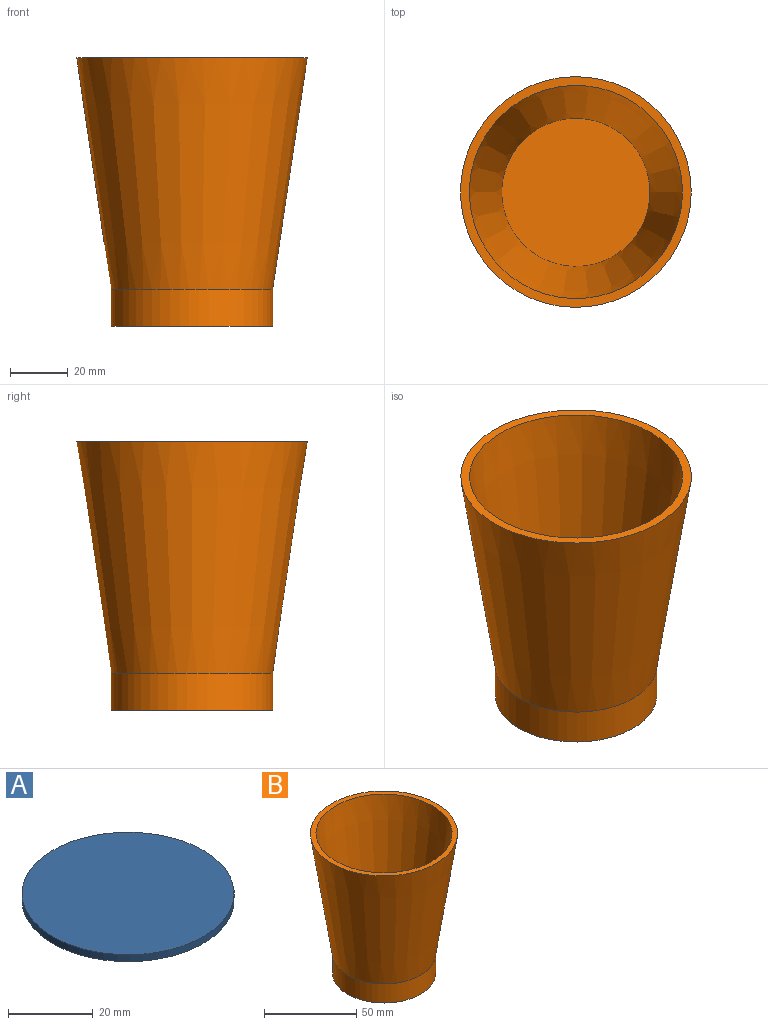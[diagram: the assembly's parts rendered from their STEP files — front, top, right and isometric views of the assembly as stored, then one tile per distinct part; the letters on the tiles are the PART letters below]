
ASSEMBLY  parts=2 mates=1
PART A: 3 faces, bbox 50x50x2 mm
  f0: cylinder r=25mm len=50mm, axis (0,0,-1), area 314.2mm2, adj f1,f2
  f1: plane 50x50mm, normal (0,0,1), area 1963.5mm2, adj f0
  f2: plane 50x50mm, normal (0,0,-1), area 1963.5mm2, adj f0
PART B: 11 faces, bbox 80x80x93 mm
  f0: cylinder r=28mm len=56mm, axis (0,0,-1), area 2234.3mm2, adj f1,f5
  f1: plane 56x56mm, normal (0,0,-1), area 499.5mm2, adj f0,f2
  f2: cylinder r=25mm len=50mm, axis (0,0,-1), area 785.4mm2, adj f1,f3
  f3: plane 50x50mm, normal (0,0,-1), area 1963.5mm2, adj f2
  f4: plane 80x80mm, normal (0,0,1), area 733.4mm2, adj f5,f6
  f5: cone r=40mm half-angle=8.5deg, axis (0,0,1), area 17344.8mm2, adj f0,f4
  f6: cone r=37.03mm half-angle=8.5deg, axis (0,0,1), area 15007.4mm2, adj f4,f7
  f7: plane 51.4x51.4mm, normal (0,0,1), area 2075mm2, adj f6
  f8: cone r=0mm half-angle=89.3deg, axis (0,0,1), area 1963.7mm2, adj f10
  f9: plane 50x50mm, normal (0,0,1), area 1963.5mm2, adj f10
  f10: cylinder r=25mm len=50mm, axis (0,0,-1), area 773.3mm2, adj f8,f9
PLACE A rot(axis=(1,0,0),180deg) t=(-48.58,-19.28,-31.34)mm
PLACE B t=(-48.58,-19.28,-36.34)mm
MATE planar A.f0 <-> B.f2  axis (0,0,1) through (-48.58,-19.28,-31.34)mm
